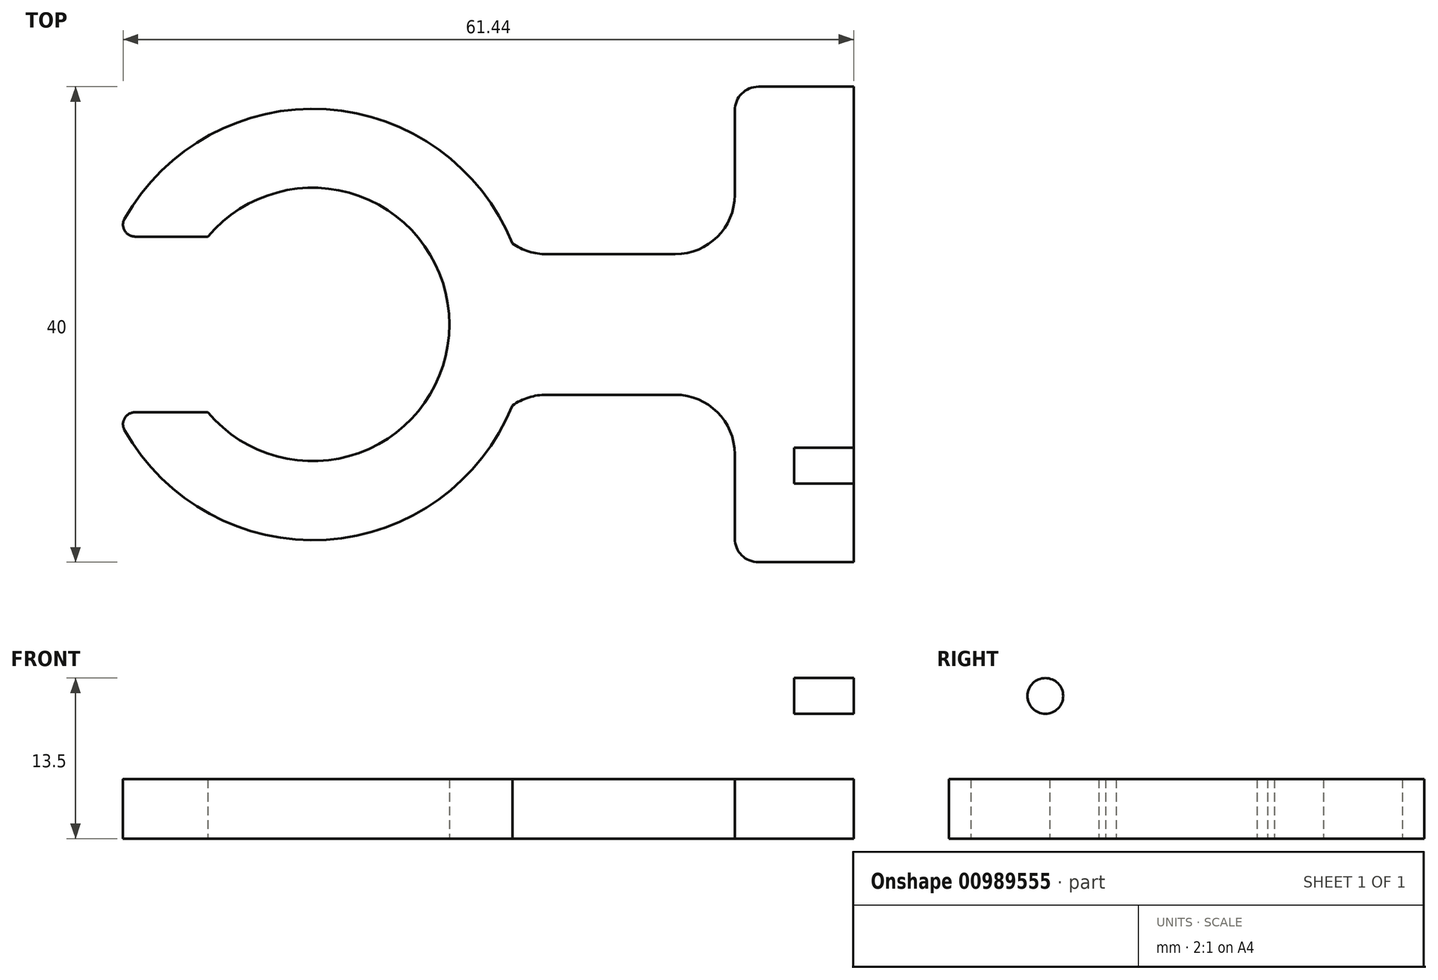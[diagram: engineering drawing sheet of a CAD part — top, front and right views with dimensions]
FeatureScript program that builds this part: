
annotation { "Feature Type Name" : "Feature", "Feature Type Description" : "" }
export const myFeature = defineFeature(function(context is Context, id is Id, definition is map)
    precondition{}
    {
        {
            var Q0;
            Q0=qCreatedBy(makeId("Top.planeOp"),FACE);
            var sketch = newSketch(context, id + "F0", { "sketchPlane" : qUnion([Q0])});
            skArc(sketch, "E0", {"start": v(-8.8, -7.4) * mm, "mid": v(11.5, 0) * mm, "end": v(-8.8, 7.4) * mm});
            skLineSegment(sketch, "E1", {"start": v(-13.9, 11.66) * mm, "end": v(-13.02, 10.93) * mm, "construction": true});
            skLineSegment(sketch, "E2.MirrorCS", {"start": v(-13.9, -11.66) * mm, "end": v(-13.02, -10.93) * mm, "construction": true});
            skLineSegment(sketch, "E3.trimOffspring", {"start": v(-13.02, 10.93) * mm, "end": v(-13.9, 11.66) * mm, "construction": true});
            skLineSegment(sketch, "E4", {"start": v(11.5, 0) * mm, "end": v(45.5, 0) * mm, "construction": true});
            skLineSegment(sketch, "E5", {"start": v(19.68, 5.91) * mm, "end": v(30.5, 5.91) * mm});
            skLineSegment(sketch, "E6", {"start": v(35.5, 10.91) * mm, "end": v(35.5, 18) * mm});
            skLineSegment(sketch, "E7", {"start": v(37.5, 20) * mm, "end": v(45.5, 20) * mm});
            skLineSegment(sketch, "E8", {"start": v(45.5, 20) * mm, "end": v(45.5, 0) * mm});
            skLineSegment(sketch, "E9.MirrorCS", {"start": v(19.68, -5.91) * mm, "end": v(30.5, -5.91) * mm});
            skLineSegment(sketch, "E10.MirrorCS", {"start": v(35.5, -10.91) * mm, "end": v(35.5, -18) * mm});
            skLineSegment(sketch, "E11.MirrorCS", {"start": v(37.5, -20) * mm, "end": v(45.5, -20) * mm});
            skLineSegment(sketch, "E12.MirrorCS", {"start": v(45.5, -20) * mm, "end": v(45.5, 0) * mm});
            skPoint(sketch, "E13.newPointB", {"position": v(16.43, 5.91) * mm});
            skArc(sketch, "E13.filletArc", {"start": v(16.81, 6.81) * mm, "mid": v(18.17, 6.14) * mm, "end": v(19.68, 5.91) * mm});
            skPoint(sketch, "E14.visualSharp", {"position": v(35.5, 5.91) * mm});
            skArc(sketch, "E14.filletArc", {"start": v(30.5, 5.91) * mm, "mid": v(34.04, 7.37) * mm, "end": v(35.5, 10.91) * mm});
            skArc(sketch, "E15.MirrorCS", {"start": v(16.81, -6.81) * mm, "mid": v(18.17, -6.14) * mm, "end": v(19.68, -5.91) * mm});
            skArc(sketch, "E16.MirrorCS", {"start": v(30.5, -5.91) * mm, "mid": v(34.04, -7.37) * mm, "end": v(35.5, -10.91) * mm});
            skPoint(sketch, "E17.orphan", {"position": v(35.5, -5.91) * mm});
            skPoint(sketch, "E18.orphan", {"position": v(16.43, -5.91) * mm});
            skPoint(sketch, "E19.visualSharp", {"position": v(35.5, 20) * mm});
            skArc(sketch, "E19.filletArc", {"start": v(37.5, 20) * mm, "mid": v(36.09, 19.41) * mm, "end": v(35.5, 18) * mm});
            skPoint(sketch, "E20.visualSharp", {"position": v(35.5, -20) * mm});
            skArc(sketch, "E20.filletArc", {"start": v(35.5, -18) * mm, "mid": v(36.09, -19.41) * mm, "end": v(37.5, -20) * mm});
            skArc(sketch, "E21", {"start": v(-13.9, -11.66) * mm, "mid": v(2.83, -17.92) * mm, "end": v(16.81, -6.81) * mm});
            skLineSegment(sketch, "E22", {"start": v(-8.8, 7.4) * mm, "end": v(-14.94, 7.4) * mm});
            skLineSegment(sketch, "E23.trimOffspring", {"start": v(-8.8, 7.4) * mm, "end": v(-5.53, 4.64) * mm, "construction": true});
            skPoint(sketch, "E24.orphan", {"position": v(-14.73, 12.36) * mm});
            skPoint(sketch, "E25.visualSharp", {"position": v(-16.56, 7.4) * mm});
            skArc(sketch, "E25.filletArc", {"start": v(-15.82, 8.88) * mm, "mid": v(-15.8, 7.89) * mm, "end": v(-14.94, 7.4) * mm});
            skLineSegment(sketch, "E26.MirrorCS", {"start": v(-8.8, -7.4) * mm, "end": v(-14.94, -7.4) * mm});
            skArc(sketch, "E27.MirrorCS", {"start": v(-15.82, -8.88) * mm, "mid": v(-15.8, -7.89) * mm, "end": v(-14.94, -7.4) * mm});
            skArc(sketch, "E28.MirrorCS", {"start": v(-13.9, 11.66) * mm, "mid": v(2.83, 17.92) * mm, "end": v(16.81, 6.81) * mm});
            skPoint(sketch, "E29.orphan", {"position": v(15.3, 8.49) * mm});
            skPoint(sketch, "E30.MirrorCS.end.orphan", {"position": v(-13.02, -10.93) * mm});
            skPoint(sketch, "E30.MirrorCS.start.orphan", {"position": v(15.3, -8.49) * mm});
            skPoint(sketch, "E31.trimOffspring.end.orphan", {"position": v(-5.53, -4.64) * mm});
            skPoint(sketch, "E32.MirrorCS.start.orphan", {"position": v(-14.73, -12.36) * mm});
            skArc(sketch, "E33.trimOffspring", {"start": v(16.81, 6.81) * mm, "mid": v(1.15, 18.1) * mm, "end": v(-15.82, 8.88) * mm});
            skArc(sketch, "E34.trimOffspring", {"start": v(16.81, -6.81) * mm, "mid": v(1.15, -18.1) * mm, "end": v(-15.82, -8.88) * mm});
            skSolve(sketch);
        }
        {
            var Q0;
            Q0=makeQuery(id+"F0.imprint","IMPRINT",FACE,{"disambiguationData":[TD([[makeQuery(id+"F0.imprint","IMPRINT",EDGE,{"derivedFrom":sQuery(id+"F0.wireOp",EDGE,"E0")}),-1.0]])]});
            extrude(context, id + "F1", {"entities" : qUnion([Q0]), "depth" : 5 * mm, "offsetDistance" : 25 * mm});
        }
        {
            var Q0;
            Q0=makeQuery(id+"F1.opExtrude","CAP_FACE",FACE,{"disambiguationData":[OSD([sQuery(id+"F0.wireOp",EDGE,"E0"),sQuery(id+"F0.wireOp",EDGE,"E5"),sQuery(id+"F0.wireOp",EDGE,"E6"),sQuery(id+"F0.wireOp",EDGE,"E7"),sQuery(id+"F0.wireOp",EDGE,"E8"),sQuery(id+"F0.wireOp",EDGE,"E9.MirrorCS"),sQuery(id+"F0.wireOp",EDGE,"E10.MirrorCS"),sQuery(id+"F0.wireOp",EDGE,"E11.MirrorCS"),sQuery(id+"F0.wireOp",EDGE,"E12.MirrorCS"),sQuery(id+"F0.wireOp",EDGE,"E13.filletArc"),sQuery(id+"F0.wireOp",EDGE,"E14.filletArc"),sQuery(id+"F0.wireOp",EDGE,"E15.MirrorCS"),sQuery(id+"F0.wireOp",EDGE,"E16.MirrorCS"),sQuery(id+"F0.wireOp",EDGE,"E19.filletArc"),sQuery(id+"F0.wireOp",EDGE,"E20.filletArc"),sQuery(id+"F0.wireOp",EDGE,"E22"),sQuery(id+"F0.wireOp",EDGE,"E25.filletArc"),sQuery(id+"F0.wireOp",EDGE,"E26.MirrorCS"),sQuery(id+"F0.wireOp",EDGE,"E27.MirrorCS"),sQuery(id+"F0.wireOp",EDGE,"E33.trimOffspring"),sQuery(id+"F0.wireOp",EDGE,"E34.trimOffspring")])],"isStart":false});
            var sketch = newSketch(context, id + "F2", { "sketchPlane" : qUnion([Q0])});
            skLineSegment(sketch, "E35.bottom", {"start": v(45.5, 20) * mm, "end": v(40.5, 20) * mm});
            skLineSegment(sketch, "E35.top", {"start": v(45.5, -20) * mm, "end": v(40.5, -20) * mm});
            skLineSegment(sketch, "E35.left", {"start": v(45.5, 20) * mm, "end": v(45.5, -20) * mm});
            skLineSegment(sketch, "E35.right", {"start": v(40.5, 20) * mm, "end": v(40.5, -20) * mm});
            skSolve(sketch);
        }
        {
            var Q0;
            Q0=makeQuery(id+"F2.imprint","IMPRINT",FACE,{"disambiguationData":[TD([[makeQuery(id+"F2.imprint","IMPRINT",EDGE,{"derivedFrom":sQuery(id+"F2.wireOp",EDGE,"E35.bottom")}),-1.0]])]});
            extrude(context, id + "F3", {"entities" : qUnion([Q0]), "operationType" : NewBodyOperationType.ADD, "depth" : 12 * mm, "offsetDistance" : 25 * mm});
        }
        {
            var Q0;
            Q0=makeQuery(id+"F3.opExtrude","CAP_EDGE",EDGE,{"disambiguationData":[OSD([sQuery(id+"F2.wireOp",EDGE,"E35.right")])],"isStart":true});
            var Q1;
            Q1=makeQuery(id+"F3.opExtrude","CAP_EDGE",EDGE,{"disambiguationData":[OSD([sQuery(id+"F2.wireOp",EDGE,"E35.bottom")])],"isStart":false});
            var Q2;
            Q2=makeQuery(id+"F3.opExtrude","CAP_EDGE",EDGE,{"disambiguationData":[OSD([sQuery(id+"F2.wireOp",EDGE,"E35.top")])],"isStart":false});
            fillet(context, id + "F4", {"entities" : qUnion([Q0, Q1, Q2]), "radius" : 3 * mm, "tangentPropagation" : true, "allowEdgeOverflow" : false});
        }
        {
            var Q0;
            Q0=makeQuery(id+"F3.opExtrude","SWEPT_FACE",FACE,{"disambiguationData":[OSD([sQuery(id+"F2.wireOp",EDGE,"E35.right")])]});
            var sketch = newSketch(context, id + "F5", { "sketchPlane" : qUnion([Q0])});
            skLineSegment(sketch, "E36", {"start": v(-20, 12) * mm, "end": v(20, 12) * mm, "construction": true});
            skLineSegment(sketch, "E37", {"start": v(0, 17) * mm, "end": v(0, 12) * mm, "construction": true});
            skCircle(sketch, "E38", {"center": v(-11.88, 12) * mm, "radius": 1.5 * mm});
            skCircle(sketch, "E39.MirrorC", {"center": v(11.88, 12) * mm, "radius": 1.5 * mm});
            skSolve(sketch);
        }
        {
            var Q0;
            Q0=makeQuery(id+"F5.imprint","IMPRINT",FACE,{"disambiguationData":[TD([[makeQuery(id+"F5.imprint","IMPRINT",EDGE,{"derivedFrom":sQuery(id+"F5.wireOp",EDGE,"E38")}),1.0]])]});
            var Q1;
            Q1=makeQuery(id+"F5.imprint","IMPRINT",FACE,{"disambiguationData":[TD([[makeQuery(id+"F5.imprint","IMPRINT",EDGE,{"derivedFrom":sQuery(id+"F5.wireOp",EDGE,"E39.MirrorC")}),-1.0]])]});
            extrude(context, id + "F6", {"entities" : qUnion([Q0, Q1]), "operationType" : NewBodyOperationType.REMOVE, "oppositeDirection" : true, "depth" : 10 * mm, "offsetDistance" : 25 * mm});
        }
    });
